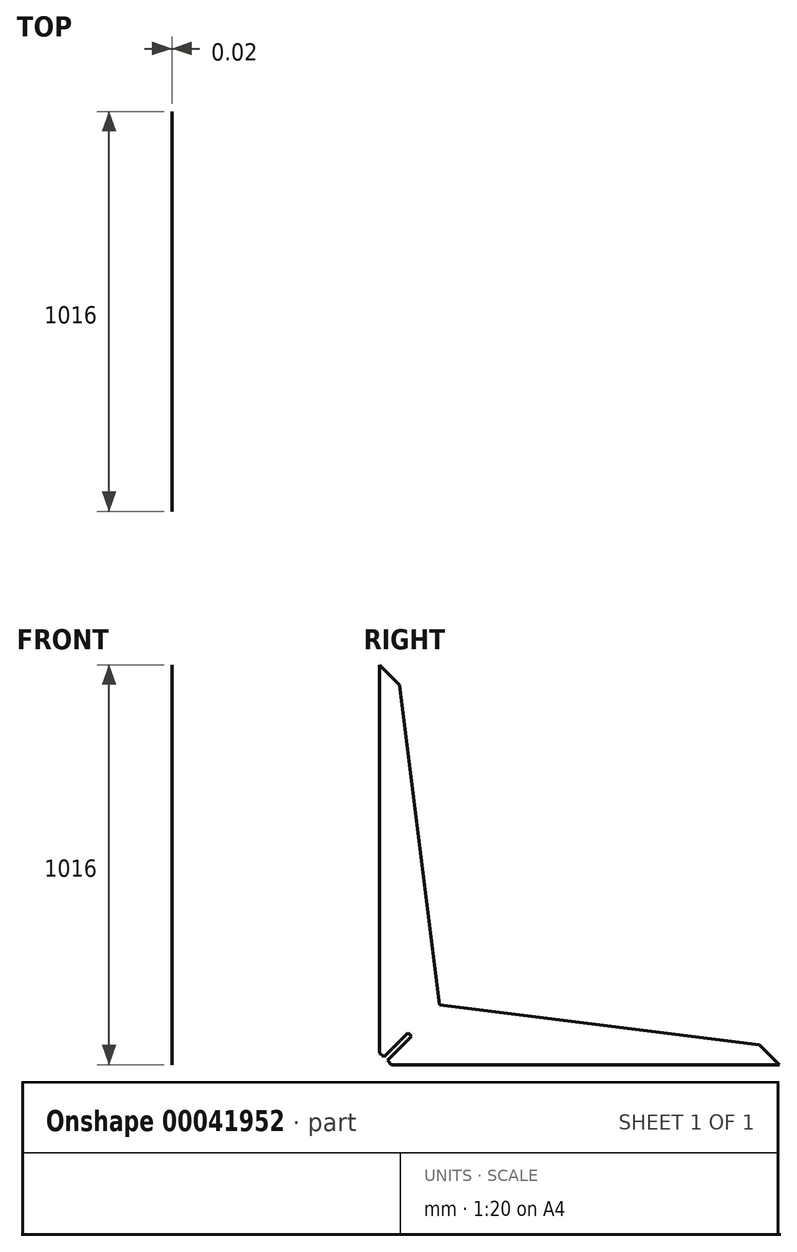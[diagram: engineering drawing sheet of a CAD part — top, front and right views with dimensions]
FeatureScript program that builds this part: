
annotation { "Feature Type Name" : "Feature", "Feature Type Description" : "" }
export const myFeature = defineFeature(function(context is Context, id is Id, definition is map)
    precondition{}
    {
        {
            var Q0;
            Q0=qCreatedBy(makeId("Right.planeOp"),FACE);
            var sketch = newSketch(context, id + "F0", { "sketchPlane" : qUnion([Q0])});
            skLineSegment(sketch, "E0", {"start": v(-364.07, 651.93) * mm, "end": v(-364.07, -364.07) * mm});
            skLineSegment(sketch, "E1", {"start": v(-364.07, -364.07) * mm, "end": v(651.93, -364.07) * mm});
            skLineSegment(sketch, "E2", {"start": v(-364.07, 651.93) * mm, "end": v(-313.27, 601.13) * mm});
            skLineSegment(sketch, "E3", {"start": v(-313.27, 601.13) * mm, "end": v(-211.67, -211.67) * mm});
            skLineSegment(sketch, "E4", {"start": v(-211.67, -211.67) * mm, "end": v(601.13, -313.27) * mm});
            skLineSegment(sketch, "E5", {"start": v(651.93, -364.07) * mm, "end": v(601.13, -313.27) * mm});
            skSolve(sketch);
        }
        {
            var Q0;
            Q0=makeQuery(id+"F0.imprint","IMPRINT",FACE,{"disambiguationData":[TD([[makeQuery(id+"F0.imprint","IMPRINT",EDGE,{"derivedFrom":sQuery(id+"F0.wireOp",EDGE,"E0")}),1.0]])]});
            extrude(context, id + "F1", {"entities" : qUnion([Q0]), "depth" : 1 / 50.8 * mm});
        }
        {
            var Q0;
            Q0=makeQuery(id+"F1.opExtrude","CAP_FACE",FACE,{"disambiguationData":[OSD([sQuery(id+"F0.wireOp",EDGE,"E0"),sQuery(id+"F0.wireOp",EDGE,"E1"),sQuery(id+"F0.wireOp",EDGE,"E2"),sQuery(id+"F0.wireOp",EDGE,"E3"),sQuery(id+"F0.wireOp",EDGE,"E4"),sQuery(id+"F0.wireOp",EDGE,"E5")])],"isStart":false});
            var sketch = newSketch(context, id + "F2", { "sketchPlane" : qUnion([Q0])});
            skLineSegment(sketch, "E6", {"start": v(-287.87, -287.87) * mm, "end": v(-292.36, -283.38) * mm});
            skLineSegment(sketch, "E7.MirrorCS", {"start": v(-287.87, -287.87) * mm, "end": v(-283.38, -292.36) * mm});
            skLineSegment(sketch, "E8", {"start": v(-292.36, -283.38) * mm, "end": v(-364.07, -355.09) * mm});
            skLineSegment(sketch, "E9", {"start": v(-364.07, -355.09) * mm, "end": v(-364.07, -364.07) * mm});
            skLineSegment(sketch, "E10", {"start": v(-283.38, -292.36) * mm, "end": v(-355.09, -364.07) * mm});
            skLineSegment(sketch, "E11", {"start": v(-355.09, -364.07) * mm, "end": v(-364.07, -364.07) * mm});
            skSolve(sketch);
        }
        {
            var Q0;
            Q0 = qSketchRegion(id + "F2", true);
            extrude(context, id + "F3", {"entities" : qUnion([Q0]), "operationType" : NewBodyOperationType.REMOVE, "endBound" : BoundingType.THROUGH_ALL, "oppositeDirection" : true, "depth" : 25.4 * mm});
        }
        {
            var Q0;
            Q0=makeQuery(id+"F1.opExtrude","CAP_FACE",FACE,{"disambiguationData":[OSD([sQuery(id+"F0.wireOp",EDGE,"E0"),sQuery(id+"F0.wireOp",EDGE,"E1"),sQuery(id+"F0.wireOp",EDGE,"E2"),sQuery(id+"F0.wireOp",EDGE,"E3"),sQuery(id+"F0.wireOp",EDGE,"E4"),sQuery(id+"F0.wireOp",EDGE,"E5")])],"isStart":false});
            var sketch = newSketch(context, id + "F4", { "sketchPlane" : qUnion([Q0])});
            skLineSegment(sketch, "E12", {"start": v(-364.07, -334.15) * mm, "end": v(-364.07, -355.09) * mm});
            skLineSegment(sketch, "E13", {"start": v(-364.07, -355.09) * mm, "end": v(-355.09, -364.07) * mm});
            skLineSegment(sketch, "E14.MirrorCS", {"start": v(-334.15, -364.07) * mm, "end": v(-355.09, -364.07) * mm});
            skLineSegment(sketch, "E15", {"start": v(-364.07, -334.15) * mm, "end": v(-334.15, -364.07) * mm});
            skSolve(sketch);
        }
        {
            var Q0;
            Q0 = qSketchRegion(id + "F4", true);
            extrude(context, id + "F5", {"entities" : qUnion([Q0]), "operationType" : NewBodyOperationType.REMOVE, "endBound" : BoundingType.THROUGH_ALL, "oppositeDirection" : true, "depth" : 25.4 * mm});
        }
    });
